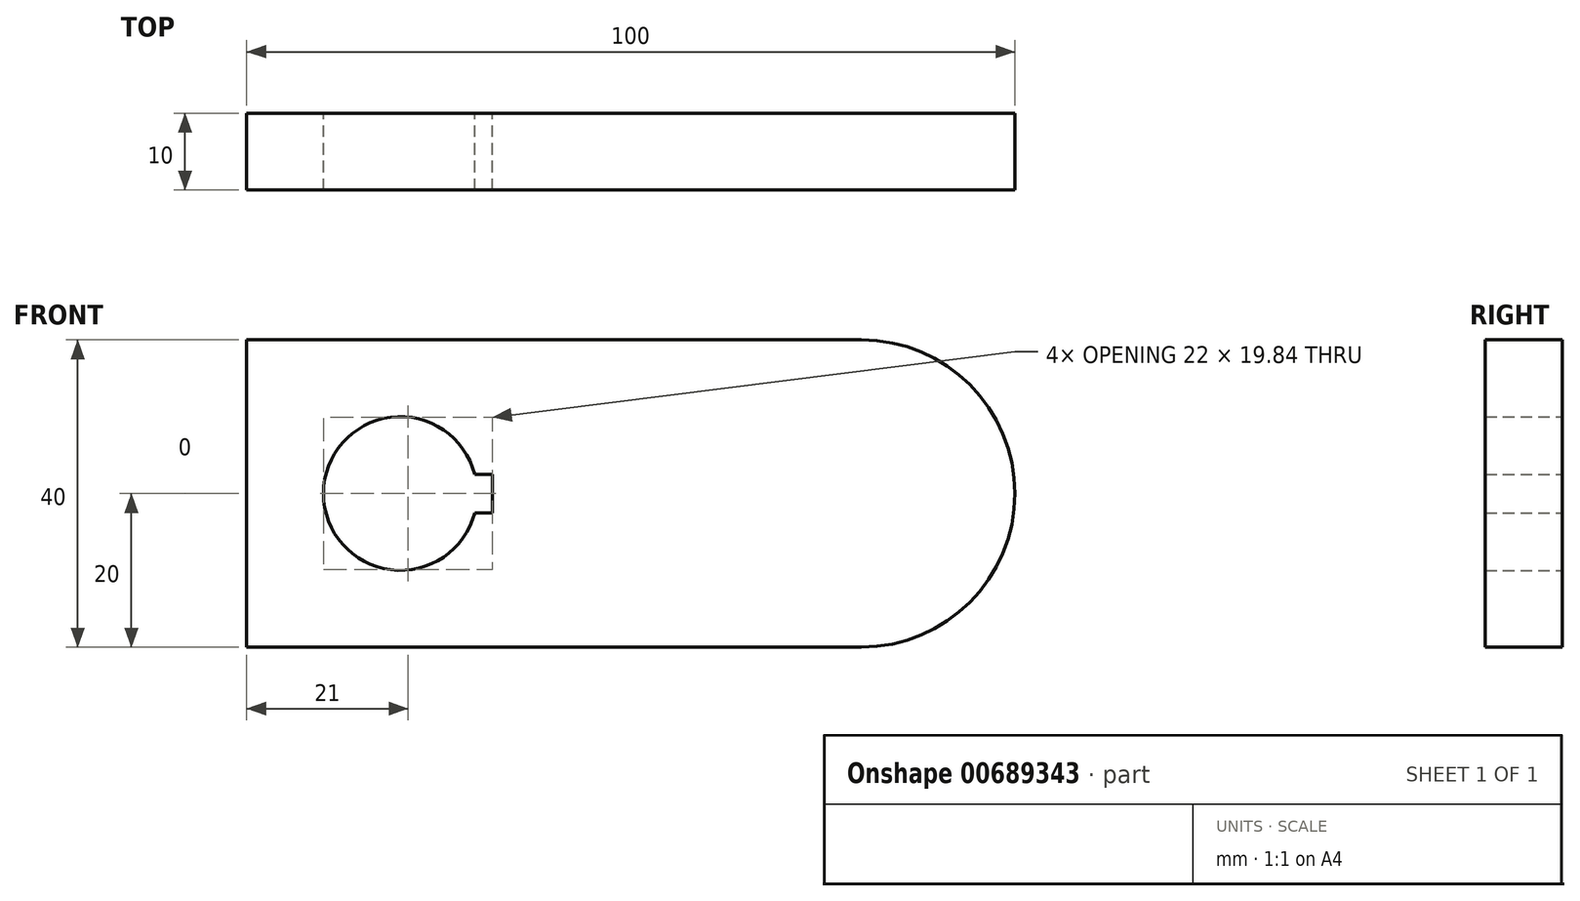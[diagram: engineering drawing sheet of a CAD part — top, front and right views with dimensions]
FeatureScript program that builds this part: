
annotation { "Feature Type Name" : "Feature", "Feature Type Description" : "" }
export const myFeature = defineFeature(function(context is Context, id is Id, definition is map)
    precondition{}
    {
        {
            var Q0;
            Q0=qCreatedBy(makeId("Front.planeOp"),FACE);
            var sketch = newSketch(context, id + "F0", { "sketchPlane" : qUnion([Q0])});
            skLineSegment(sketch, "E0.bottom", {"start": v(-80, 40) * mm, "end": v(0, 40) * mm});
            skLineSegment(sketch, "E0.top", {"start": v(-80, 0) * mm, "end": v(0, 0) * mm});
            skLineSegment(sketch, "E0.left", {"start": v(-80, 40) * mm, "end": v(-80, 0) * mm});
            skArc(sketch, "E1", {"start": v(-50.32, 22.5) * mm, "mid": v(-70, 20) * mm, "end": v(-50.32, 17.5) * mm});
            skPoint(sketch, "E2.centerSnap0", {"position": v(0, 20) * mm});
            skArc(sketch, "E3", {"start": v(0, 0) * mm, "mid": v(20, 20) * mm, "end": v(0, 40) * mm});
            skLineSegment(sketch, "E4", {"start": v(-60, 20) * mm, "end": v(-48, 20) * mm, "construction": true});
            skLineSegment(sketch, "E5", {"start": v(-48, 20) * mm, "end": v(-48, 22.5) * mm});
            skLineSegment(sketch, "E6", {"start": v(-48, 20) * mm, "end": v(-48, 17.5) * mm});
            skLineSegment(sketch, "E7", {"start": v(-48, 22.5) * mm, "end": v(-50.32, 22.5) * mm});
            skLineSegment(sketch, "E8", {"start": v(-48, 17.5) * mm, "end": v(-50.32, 17.5) * mm});
            skSolve(sketch);
        }
        {
            var Q0;
            Q0=qSketchRegion(id+"F0",true);
            extrude(context, id + "F1", {"entities" : qUnion([Q0]), "depth" : 10 * mm, "offsetDistance" : 25 * mm});
        }
    });
